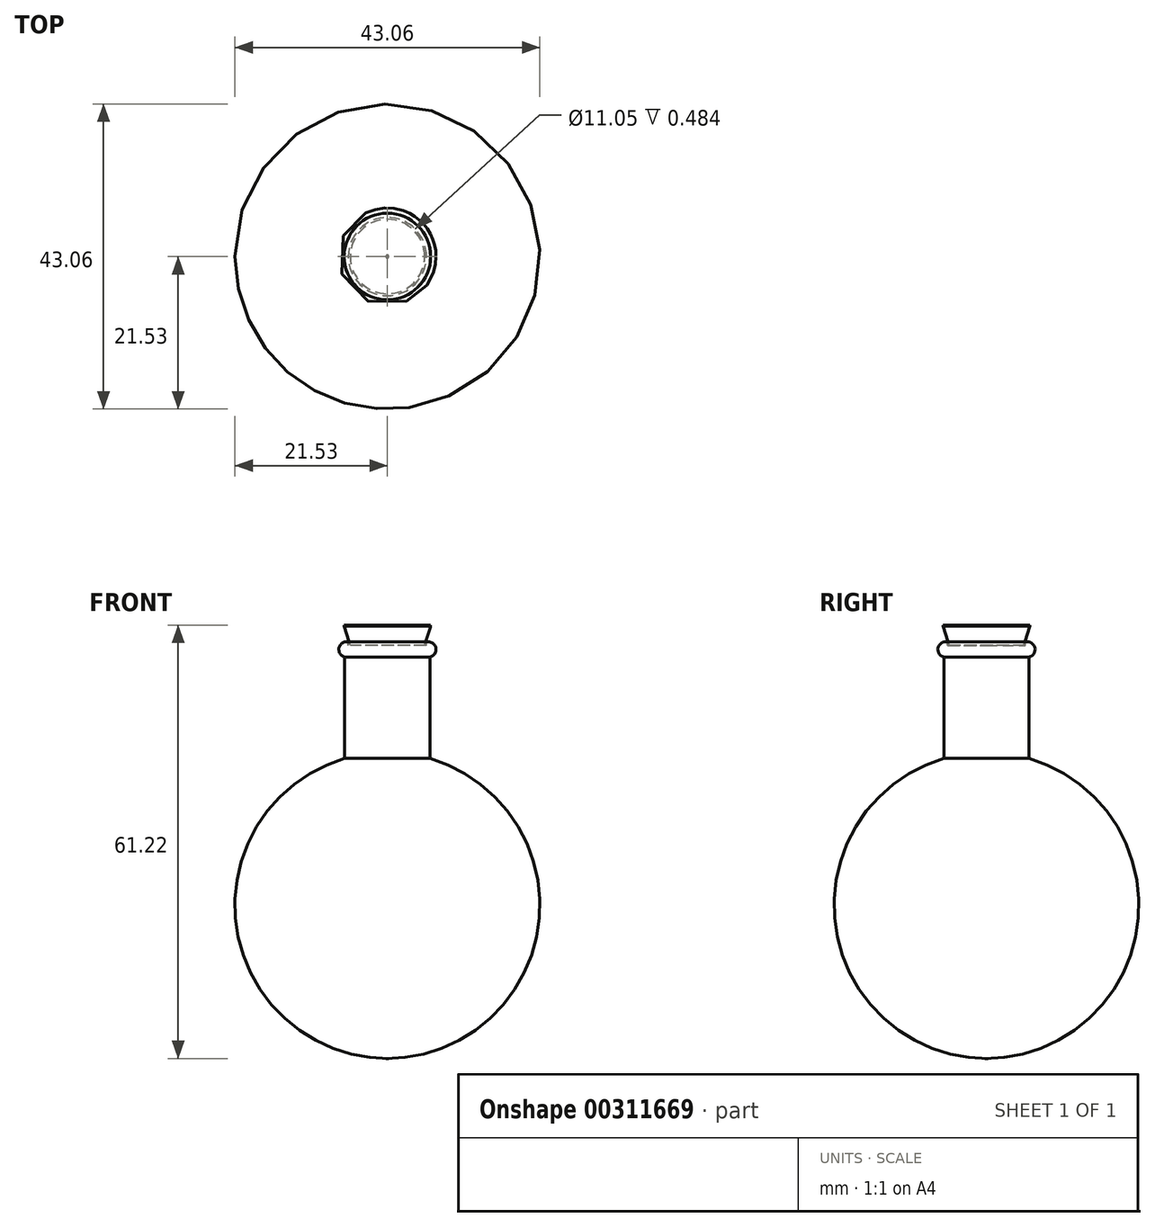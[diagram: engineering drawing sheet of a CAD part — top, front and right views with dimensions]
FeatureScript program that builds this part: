
annotation { "Feature Type Name" : "Feature", "Feature Type Description" : "" }
export const myFeature = defineFeature(function(context is Context, id is Id, definition is map)
    precondition{}
    {
        {
            var Q0;
            Q0=qCreatedBy(makeId("Front.planeOp"),FACE);
            var sketch = newSketch(context, id + "F0", { "sketchPlane" : qUnion([Q0])});
            skLineSegment(sketch, "E0", {"start": v(0, 18.83) * mm, "end": v(0, -42.39) * mm});
            skArc(sketch, "E1", {"start": v(-6.02, 0) * mm, "mid": v(-21.32, -23.8) * mm, "end": v(0, -42.39) * mm});
            skLineSegment(sketch, "E2", {"start": v(-6.02, 0) * mm, "end": v(-6.02, 14.3) * mm});
            skArc(sketch, "E3", {"start": v(-5.52, 16.43) * mm, "mid": v(-6.83, 15.62) * mm, "end": v(-6.02, 14.3) * mm});
            skLineSegment(sketch, "E4", {"start": v(-5.52, 16.43) * mm, "end": v(-5.52, 15.95) * mm});
            skLineSegment(sketch, "E5", {"start": v(-5.52, 15.95) * mm, "end": v(-5.25, 15.95) * mm});
            skLineSegment(sketch, "E6", {"start": v(-5.25, 15.95) * mm, "end": v(-6.11, 18.67) * mm});
            skLineSegment(sketch, "E7", {"start": v(-6.11, 18.83) * mm, "end": v(0, 18.83) * mm});
            skLineSegment(sketch, "E8", {"start": v(-6.11, 18.83) * mm, "end": v(-6.11, 18.67) * mm});
            skSolve(sketch);
        }
        {
            var Q0;
            Q0 = qSketchRegion(id + "F0", true);
            var Q1;
            Q1=sQuery(id+"F0.wireOp",EDGE,"E0");
            revolve(context, id + "F1", {"entities" : qUnion([Q0]), "axis" : qUnion([Q1]), "revolveType" : RevolveType.FULL});
        }
    });
